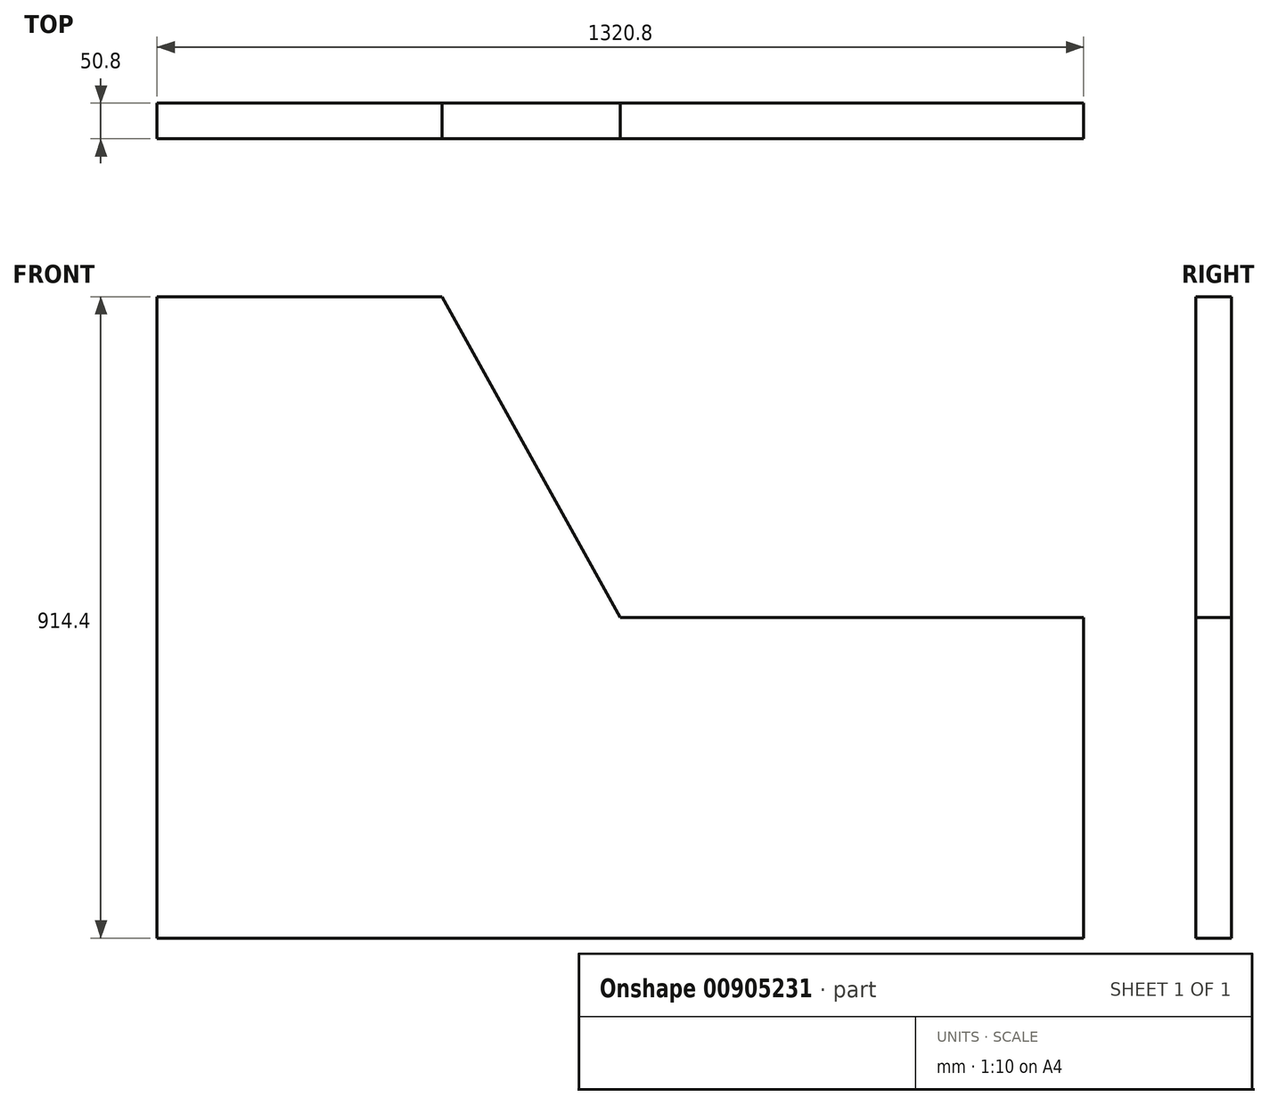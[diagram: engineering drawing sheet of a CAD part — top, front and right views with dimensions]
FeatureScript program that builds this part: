
annotation { "Feature Type Name" : "Feature", "Feature Type Description" : "" }
export const myFeature = defineFeature(function(context is Context, id is Id, definition is map)
    precondition{}
    {
        {
            var Q0;
            Q0=qCreatedBy(makeId("Front.planeOp"),FACE);
            var sketch = newSketch(context, id + "F0", { "sketchPlane" : qUnion([Q0])});
            skLineSegment(sketch, "E0", {"start": v(-1320.8, -228.6) * mm, "end": v(0, -228.6) * mm});
            skLineSegment(sketch, "E1", {"start": v(0, -228.6) * mm, "end": v(0, 228.6) * mm});
            skLineSegment(sketch, "E2", {"start": v(0, 228.6) * mm, "end": v(-660.4, 228.6) * mm});
            skLineSegment(sketch, "E3", {"start": v(-1320.8, -228.6) * mm, "end": v(-1320.8, 685.8) * mm});
            skLineSegment(sketch, "E4", {"start": v(-1320.8, 685.8) * mm, "end": v(-914.4, 685.8) * mm});
            skLineSegment(sketch, "E5", {"start": v(-914.4, 685.8) * mm, "end": v(-660.4, 228.6) * mm});
            skPoint(sketch, "E6", {"position": v(0, 0) * mm});
            skSolve(sketch);
        }
        {
            var Q0;
            Q0 = qSketchRegion(id + "F0", true);
            extrude(context, id + "F1", {"entities" : qUnion([Q0]), "endBound" : BoundingType.SYMMETRIC, "depth" : 50.8 * mm, "offsetDistance" : 25.4 * mm});
        }
    });
